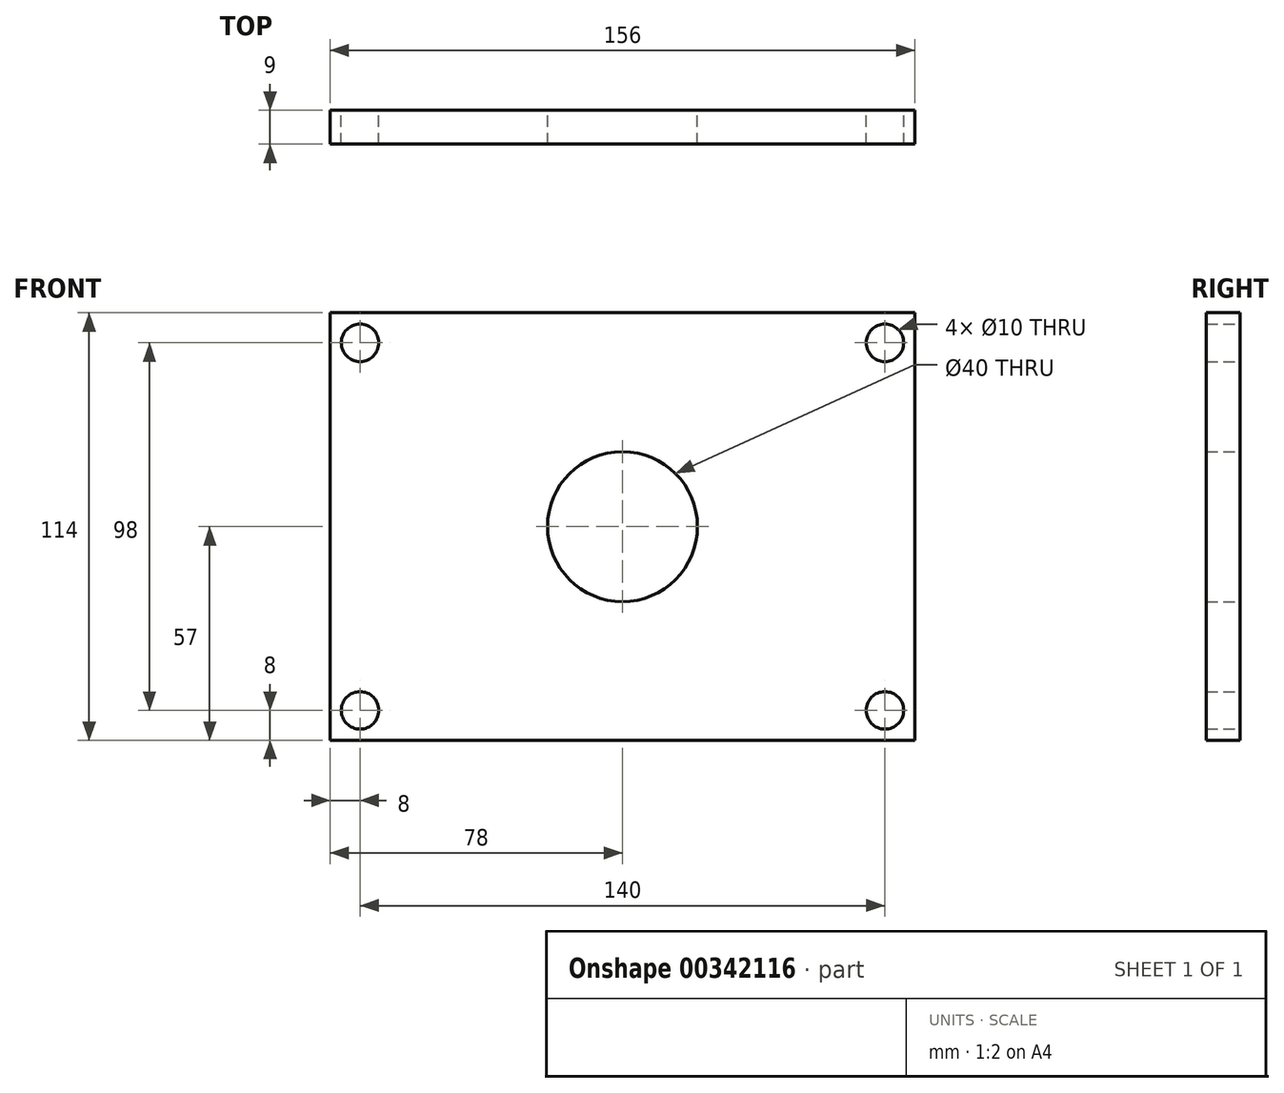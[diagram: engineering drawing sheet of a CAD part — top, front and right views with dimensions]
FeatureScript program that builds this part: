
annotation { "Feature Type Name" : "Feature", "Feature Type Description" : "" }
export const myFeature = defineFeature(function(context is Context, id is Id, definition is map)
    precondition{}
    {
        {
            var Q0;
            Q0=qCreatedBy(makeId("Front.planeOp"),FACE);
            var sketch = newSketch(context, id + "F0", { "sketchPlane" : qUnion([Q0])});
            skCircle(sketch, "E0", {"center": v(0, 0) * mm, "radius": 20 * mm});
            skLineSegment(sketch, "E1.bottom", {"start": v(-78, -57) * mm, "end": v(78, -57) * mm});
            skLineSegment(sketch, "E1.top", {"start": v(-78, 57) * mm, "end": v(78, 57) * mm});
            skLineSegment(sketch, "E1.left", {"start": v(-78, -57) * mm, "end": v(-78, 57) * mm});
            skLineSegment(sketch, "E1.right", {"start": v(78, -57) * mm, "end": v(78, 57) * mm});
            skLineSegment(sketch, "E2", {"start": v(-78, 57) * mm, "end": v(-78, 52) * mm});
            skLineSegment(sketch, "E3.MirrorCS", {"start": v(78, 57) * mm, "end": v(-78, 57) * mm});
            skLineSegment(sketch, "E4.MirrorCS", {"start": v(78, 57) * mm, "end": v(78, 52) * mm});
            skLineSegment(sketch, "E5.MirrorCS", {"start": v(78, -57) * mm, "end": v(78, -52) * mm});
            skLineSegment(sketch, "E6.MirrorCS", {"start": v(-78, -57) * mm, "end": v(-78, -52) * mm});
            skLineSegment(sketch, "E7.MirrorCS", {"start": v(78, -57) * mm, "end": v(-78, -57) * mm});
            skLineSegment(sketch, "E8.bottom", {"start": v(-70, 49) * mm, "end": v(70, 49) * mm, "construction": true});
            skLineSegment(sketch, "E8.top", {"start": v(-70, -49) * mm, "end": v(70, -49) * mm, "construction": true});
            skLineSegment(sketch, "E8.left", {"start": v(-70, 49) * mm, "end": v(-70, -49) * mm, "construction": true});
            skLineSegment(sketch, "E8.right", {"start": v(70, 49) * mm, "end": v(70, -49) * mm, "construction": true});
            skCircle(sketch, "E9", {"center": v(70, 49) * mm, "radius": 5 * mm});
            skCircle(sketch, "E10", {"center": v(-70, 49) * mm, "radius": 5 * mm});
            skCircle(sketch, "E11", {"center": v(70, -49) * mm, "radius": 5 * mm});
            skCircle(sketch, "E12", {"center": v(-70, -49) * mm, "radius": 5 * mm});
            skSolve(sketch);
        }
        {
            var Q0;
            Q0=qSketchRegion(id+"F0",true);
            extrude(context, id + "F1", {"entities" : qUnion([Q0]), "depth" : 9 * mm});
        }
    });
